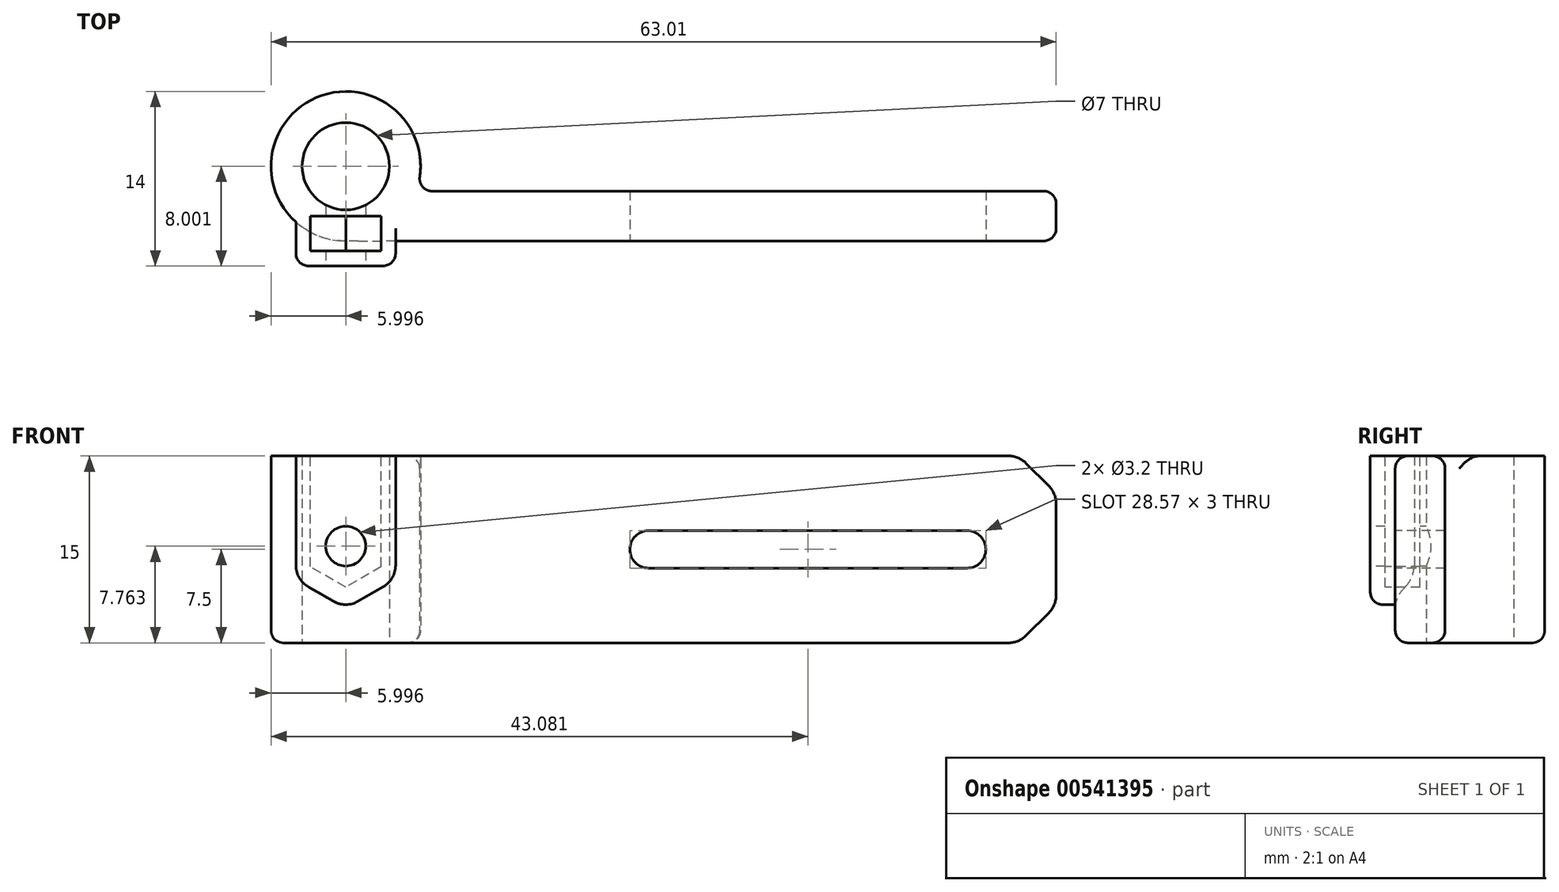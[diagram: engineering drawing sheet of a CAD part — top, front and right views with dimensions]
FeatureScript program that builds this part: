
annotation { "Feature Type Name" : "Feature", "Feature Type Description" : "" }
export const myFeature = defineFeature(function(context is Context, id is Id, definition is map)
    precondition{}
    {
        {
            var Q0;
            Q0=qCreatedBy(makeId("Top.planeOp"),FACE);
            var sketch = newSketch(context, id + "F0", { "sketchPlane" : qUnion([Q0])});
            skCircle(sketch, "E0", {"center": v(-30.85, 2.7) * mm, "radius": 3.5 * mm});
            skCircle(sketch, "E1", {"center": v(-30.85, 2.7) * mm, "radius": 6 * mm});
            skLineSegment(sketch, "E2", {"start": v(-30.85, -3.3) * mm, "end": v(26.16, -3.3) * mm});
            skLineSegment(sketch, "E3", {"start": v(26.16, -3.3) * mm, "end": v(26.16, 0.7) * mm});
            skLineSegment(sketch, "E4", {"start": v(26.16, 0.7) * mm, "end": v(-25.2, 0.7) * mm});
            skSolve(sketch);
        }
        {
            var Q0;
            {var subQ0=sQuery(id+"F0.wireOp",EDGE,"E2");Q0=makeQuery(id+"F0.imprint","IMPRINT",FACE,{"disambiguationData":[TD([[makeQuery(id+"F0.imprint","IMPRINT",EDGE,{"derivedFrom":subQ0}),1.0]])]});}
            var Q1;
            Q1=makeQuery(id+"F0.imprint","IMPRINT",FACE,{"disambiguationData":[TD([[makeQuery(id+"F0.imprint","IMPRINT",EDGE,{"derivedFrom":sQuery(id+"F0.wireOp",EDGE,"E0")}),-1.0]])]});
            extrude(context, id + "F1", {"entities" : qUnion([Q0, Q1]), "depth" : 15 * mm});
        }
        {
            var Q0;
            Q0=makeQuery(id+"F1.opExtrude","SWEPT_FACE",FACE,{"disambiguationData":[OSD([sQuery(id+"F0.wireOp",EDGE,"E2")])]});
            var sketch = newSketch(context, id + "F2", { "sketchPlane" : qUnion([Q0])});
            skCircle(sketch, "E5.cCircle", {"center": v(-30.85, 7.38) * mm, "radius": 4 * mm, "construction": true});
            skLineSegment(sketch, "E5.0", {"start": v(-26.85, 9.7) * mm, "end": v(-26.85, 5.07) * mm});
            skLineSegment(sketch, "E5.1", {"start": v(-26.85, 5.07) * mm, "end": v(-30.85, 2.76) * mm});
            skLineSegment(sketch, "E5.2", {"start": v(-30.85, 2.76) * mm, "end": v(-34.85, 5.07) * mm});
            skLineSegment(sketch, "E5.3", {"start": v(-34.85, 5.07) * mm, "end": v(-34.85, 9.7) * mm});
            skLineSegment(sketch, "E5.4", {"start": v(-34.85, 9.7) * mm, "end": v(-30.85, 12) * mm});
            skLineSegment(sketch, "E5.5", {"start": v(-30.85, 12) * mm, "end": v(-26.85, 9.7) * mm});
            skPoint(sketch, "E5.0.midPoint", {"position": v(-26.85, 7.38) * mm});
            skLineSegment(sketch, "E6", {"start": v(-34.85, 9.7) * mm, "end": v(-34.85, 15) * mm});
            skLineSegment(sketch, "E7", {"start": v(-34.85, 15) * mm, "end": v(-26.85, 15) * mm});
            skLineSegment(sketch, "E8", {"start": v(-26.85, 15) * mm, "end": v(-26.85, 9.7) * mm});
            skSolve(sketch);
        }
        {
            var Q0;
            Q0=makeQuery(id+"F2.imprint","IMPRINT",FACE,{"disambiguationData":[TD([[makeQuery(id+"F2.imprint","IMPRINT",EDGE,{"derivedFrom":sQuery(id+"F2.wireOp",EDGE,"E5.0")}),-1.0]])]});
            var Q1;
            {var subQ0=sQuery(id+"F2.wireOp",EDGE,"E5.2");Q1=makeQuery(id+"F2.imprint","IMPRINT",FACE,{"disambiguationData":[TD([[makeQuery(id+"F2.imprint","IMPRINT",EDGE,{"derivedFrom":subQ0}),-1.0]])]});}
            var Q2;
            {var subQ0=sQuery(id+"F2.wireOp",EDGE,"E5.5");Q2=makeQuery(id+"F2.imprint","IMPRINT",FACE,{"disambiguationData":[TD([[makeQuery(id+"F2.imprint","IMPRINT",EDGE,{"derivedFrom":subQ0}),1.0]])]});}
            var Q3;
            {var subQ0=sQuery(id+"F2.wireOp",EDGE,"E5.4");Q3=makeQuery(id+"F2.imprint","IMPRINT",FACE,{"disambiguationData":[TD([[makeQuery(id+"F2.imprint","IMPRINT",EDGE,{"derivedFrom":subQ0}),1.0]])]});}
            extrude(context, id + "F3", {"entities" : qUnion([Q0, Q1, Q2, Q3]), "operationType" : NewBodyOperationType.ADD, "oppositeDirection" : true, "depth" : 2 * mm, "hasSecondDirection" : true, "secondDirectionOppositeDirection" : false, "secondDirectionDepth" : 2 * mm});
        }
        {
            var Q0;
            Q0=makeQuery(id+"F3.opExtrude","CAP_FACE",FACE,{"disambiguationData":[OSD([sQuery(id+"F2.wireOp",EDGE,"E5.0"),sQuery(id+"F2.wireOp",EDGE,"E5.1"),sQuery(id+"F2.wireOp",EDGE,"E5.2"),sQuery(id+"F2.wireOp",EDGE,"E5.3"),sQuery(id+"F2.wireOp",EDGE,"E6"),sQuery(id+"F2.wireOp",EDGE,"E7"),sQuery(id+"F2.wireOp",EDGE,"E8")])],"isStart":true});
            var sketch = newSketch(context, id + "F4", { "sketchPlane" : qUnion([Q0])});
            skCircle(sketch, "E9.cCircle", {"center": v(-30.85, 7.76) * mm, "radius": 2.85 * mm, "construction": true});
            skLineSegment(sketch, "E9.0", {"start": v(-28, 9.4) * mm, "end": v(-28, 6.12) * mm});
            skLineSegment(sketch, "E9.1", {"start": v(-28, 6.12) * mm, "end": v(-30.85, 4.47) * mm});
            skLineSegment(sketch, "E9.2", {"start": v(-30.85, 4.47) * mm, "end": v(-33.7, 6.12) * mm});
            skLineSegment(sketch, "E9.3", {"start": v(-33.7, 6.12) * mm, "end": v(-33.7, 9.4) * mm});
            skLineSegment(sketch, "E9.4", {"start": v(-33.7, 9.4) * mm, "end": v(-30.85, 11.05) * mm});
            skLineSegment(sketch, "E9.5", {"start": v(-30.85, 11.05) * mm, "end": v(-28, 9.4) * mm});
            skPoint(sketch, "E9.0.midPoint", {"position": v(-28, 7.76) * mm});
            skLineSegment(sketch, "E10", {"start": v(-33.7, 9.4) * mm, "end": v(-33.7, 15) * mm});
            skLineSegment(sketch, "E11", {"start": v(-28, 9.4) * mm, "end": v(-28, 15) * mm});
            skSolve(sketch);
        }
        {
            var Q0;
            Q0=makeQuery(id+"F4.imprint","IMPRINT",FACE,{"disambiguationData":[TD([[makeQuery(id+"F4.imprint","IMPRINT",EDGE,{"derivedFrom":sQuery(id+"F4.wireOp",EDGE,"E9.4")}),1.0]])]});
            var Q1;
            Q1=makeQuery(id+"F4.imprint","IMPRINT",FACE,{"disambiguationData":[TD([[makeQuery(id+"F4.imprint","IMPRINT",EDGE,{"derivedFrom":sQuery(id+"F4.wireOp",EDGE,"E9.0")}),-1.0]])]});
            extrude(context, id + "F5", {"entities" : qUnion([Q0, Q1]), "operationType" : NewBodyOperationType.REMOVE, "oppositeDirection" : true, "depth" : 4 * mm, "hasSecondDirection" : true, "secondDirectionOppositeDirection" : true, "secondDirectionDepth" : 1.2 * mm});
        }
        {
            var Q0;
            Q0=sQuery(id+"F4.wireOp",VERTEX,"E9.cCircle.center");
            var Q1;
            Q1=makeQuery(id+"F1.opExtrude","SWEPT_BODY",BODY,{"disambiguationData":[OSD([sQuery(id+"F0.wireOp",EDGE,"E0"),sQuery(id+"F0.wireOp",EDGE,"E1"),sQuery(id+"F0.wireOp",EDGE,"E2"),sQuery(id+"F0.wireOp",EDGE,"E3"),sQuery(id+"F0.wireOp",EDGE,"E4")])]});
            hole(context, id + "F6", {"style" : HoleStyle.SIMPLE, "endStyle" : HoleEndStyle.BLIND, "holeDiameter" : 3.2 * mm, "holeDepth" : 8 * mm, "tappedDepth" : 12 * mm, "tapClearance" : 3, "startFromSketch" : true, "locations" : qUnion([Q0]), "scope" : qUnion([Q1])});
        }
        {
            var Q0;
            Q0=makeQuery(id+"F1.opExtrude","SWEPT_FACE",FACE,{"disambiguationData":[OSD([sQuery(id+"F0.wireOp",EDGE,"E2")])]});
            var sketch = newSketch(context, id + "F7", { "sketchPlane" : qUnion([Q0])});
            skCircle(sketch, "E12", {"center": v(-6.56, 7.5) * mm, "radius": 1.5 * mm});
            skPoint(sketch, "E12.centerSnap0", {"position": v(26.16, 7.5) * mm});
            skCircle(sketch, "E13", {"center": v(19.02, 7.5) * mm, "radius": 1.5 * mm});
            skLineSegment(sketch, "E14", {"start": v(-6.56, 6) * mm, "end": v(19.02, 6) * mm});
            skLineSegment(sketch, "E15", {"start": v(-6.56, 9) * mm, "end": v(19.02, 9) * mm});
            skSolve(sketch);
        }
        {
            var Q0;
            {var subQ0=sQuery(id+"F7.wireOp",EDGE,"E13");var subQ1=makeQuery(id+"F7.imprint","INTERSECT",VERTEX,{"derivedFrom":[subQ0,sQuery(id+"F7.wireOp",EDGE,"E14")]});Q0=makeQuery(id+"F7.imprint","IMPRINT",FACE,{"disambiguationData":[TD([[makeQuery(id+"F7.imprint","IMPRINT",EDGE,{"disambiguationData":[TD([[subQ1,1.0]])],"derivedFrom":subQ0}),1.0]])]});}
            var Q1;
            {var subQ0=sQuery(id+"F7.wireOp",EDGE,"E12");var subQ1=makeQuery(id+"F7.imprint","INTERSECT",VERTEX,{"derivedFrom":[subQ0,sQuery(id+"F7.wireOp",EDGE,"E14")]});Q1=makeQuery(id+"F7.imprint","IMPRINT",FACE,{"disambiguationData":[TD([[makeQuery(id+"F7.imprint","IMPRINT",EDGE,{"disambiguationData":[TD([[subQ1,1.0]])],"derivedFrom":subQ0}),1.0]])]});}
            var Q2;
            {var subQ0=sQuery(id+"F7.wireOp",EDGE,"E14");Q2=makeQuery(id+"F7.imprint","IMPRINT",FACE,{"disambiguationData":[TD([[makeQuery(id+"F7.imprint","IMPRINT",EDGE,{"derivedFrom":subQ0}),1.0]])]});}
            extrude(context, id + "F8", {"entities" : qUnion([Q0, Q1, Q2]), "operationType" : NewBodyOperationType.REMOVE, "oppositeDirection" : true, "depth" : 25 * mm});
        }
        {
            var Q0;
            Q0=makeQuery(id+"F1.opExtrude","CAP_EDGE",EDGE,{"disambiguationData":[OSD([sQuery(id+"F0.wireOp",EDGE,"E3")])],"isStart":false});
            var Q1;
            Q1=makeQuery(id+"F1.opExtrude","CAP_EDGE",EDGE,{"disambiguationData":[OSD([sQuery(id+"F0.wireOp",EDGE,"E3")])],"isStart":true});
            chamfer(context, id + "F9", {"entities" : qUnion([Q0, Q1]), "width" : 3 * mm, "tangentPropagation" : true});
        }
        {
            var Q0;
            Q0=makeQuery(id+"F3.opExtrude","SWEPT_EDGE",EDGE,{"disambiguationData":[OSD([sQuery(id+"F2.wireOp",EDGE,"E5.2"),sQuery(id+"F2.wireOp",EDGE,"E5.3")])]});
            var Q1;
            Q1=makeQuery(id+"F3.opExtrude","SWEPT_EDGE",EDGE,{"disambiguationData":[OSD([sQuery(id+"F0.wireOp",EDGE,"E1"),sQuery(id+"F0.wireOp",EDGE,"E2"),sQuery(id+"F2.wireOp",EDGE,"E5.1"),sQuery(id+"F2.wireOp",EDGE,"E5.2")])]});
            var Q2;
            Q2=makeQuery(id+"F3.opExtrude","SWEPT_EDGE",EDGE,{"disambiguationData":[OSD([sQuery(id+"F2.wireOp",EDGE,"E5.0"),sQuery(id+"F2.wireOp",EDGE,"E5.1")])]});
            var Q3;
            {var subQ0=sQuery(id+"F0.wireOp",EDGE,"E3");Q3=makeQuery(id+"F9.opChamfer","BLEND_EDGE",EDGE,{"blendedFrom":[makeQuery(id+"F1.opExtrude","CAP_EDGE",EDGE,{"disambiguationData":[OSD([subQ0])],"isStart":true}),makeQuery(id+"F1.opExtrude","CAP_FACE",FACE,{"disambiguationData":[OSD([sQuery(id+"F0.wireOp",EDGE,"E0"),sQuery(id+"F0.wireOp",EDGE,"E1"),sQuery(id+"F0.wireOp",EDGE,"E2"),subQ0,sQuery(id+"F0.wireOp",EDGE,"E4")])],"isStart":true})],"blendedInto":[makeQuery(id+"F1.opExtrude","CAP_FACE",FACE,{"disambiguationData":[OSD([sQuery(id+"F0.wireOp",EDGE,"E0"),sQuery(id+"F0.wireOp",EDGE,"E1"),sQuery(id+"F0.wireOp",EDGE,"E2"),subQ0,sQuery(id+"F0.wireOp",EDGE,"E4")])],"isStart":true})]});}
            var Q4;
            {var subQ0=sQuery(id+"F0.wireOp",EDGE,"E3");Q4=makeQuery(id+"F9.opChamfer","BLEND_EDGE",EDGE,{"blendedFrom":[makeQuery(id+"F1.opExtrude","CAP_EDGE",EDGE,{"disambiguationData":[OSD([subQ0])],"isStart":true}),makeQuery(id+"F1.opExtrude","SWEPT_FACE",FACE,{"disambiguationData":[OSD([subQ0])]})],"blendedInto":[makeQuery(id+"F1.opExtrude","SWEPT_FACE",FACE,{"disambiguationData":[OSD([subQ0])]})]});}
            var Q5;
            {var subQ0=sQuery(id+"F0.wireOp",EDGE,"E3");Q5=makeQuery(id+"F9.opChamfer","BLEND_EDGE",EDGE,{"blendedFrom":[makeQuery(id+"F1.opExtrude","CAP_EDGE",EDGE,{"disambiguationData":[OSD([subQ0])],"isStart":false}),makeQuery(id+"F1.opExtrude","SWEPT_FACE",FACE,{"disambiguationData":[OSD([subQ0])]})],"blendedInto":[makeQuery(id+"F1.opExtrude","SWEPT_FACE",FACE,{"disambiguationData":[OSD([subQ0])]})]});}
            var Q6;
            {var subQ0=sQuery(id+"F0.wireOp",EDGE,"E3");Q6=makeQuery(id+"F9.opChamfer","BLEND_EDGE",EDGE,{"blendedFrom":[makeQuery(id+"F1.opExtrude","CAP_EDGE",EDGE,{"disambiguationData":[OSD([subQ0])],"isStart":false}),makeQuery(id+"F3.boolean.opBoolean","MERGE",FACE,{"derivedFrom":[makeQuery(id+"F1.opExtrude","CAP_FACE",FACE,{"disambiguationData":[OSD([sQuery(id+"F0.wireOp",EDGE,"E0"),sQuery(id+"F0.wireOp",EDGE,"E1"),sQuery(id+"F0.wireOp",EDGE,"E2"),subQ0,sQuery(id+"F0.wireOp",EDGE,"E4")])],"isStart":false}),makeQuery(id+"F3.opExtrude","SWEPT_FACE",FACE,{"disambiguationData":[OSD([sQuery(id+"F2.wireOp",EDGE,"E7")])]})]})],"blendedInto":[makeQuery(id+"F3.boolean.opBoolean","MERGE",FACE,{"derivedFrom":[makeQuery(id+"F1.opExtrude","CAP_FACE",FACE,{"disambiguationData":[OSD([sQuery(id+"F0.wireOp",EDGE,"E0"),sQuery(id+"F0.wireOp",EDGE,"E1"),sQuery(id+"F0.wireOp",EDGE,"E2"),subQ0,sQuery(id+"F0.wireOp",EDGE,"E4")])],"isStart":false}),makeQuery(id+"F3.opExtrude","SWEPT_FACE",FACE,{"disambiguationData":[OSD([sQuery(id+"F2.wireOp",EDGE,"E7")])]})]})]});}
            fillet(context, id + "F10", {"entities" : qUnion([Q0, Q1, Q2, Q3, Q4, Q5, Q6]), "radius" : 2 * mm, "tangentPropagation" : true, "allowEdgeOverflow" : false});
        }
        {
            var Q0;
            Q0=makeQuery(id+"F3.opExtrude","CAP_EDGE",EDGE,{"disambiguationData":[OSD([sQuery(id+"F2.wireOp",EDGE,"E5.3"),sQuery(id+"F2.wireOp",EDGE,"E6")])],"isStart":true});
            var Q1;
            Q1=makeQuery(id+"F1.opExtrude","CAP_EDGE",EDGE,{"disambiguationData":[OSD([sQuery(id+"F0.wireOp",EDGE,"E2")])],"isStart":false});
            var Q2;
            Q2=makeQuery(id+"F1.opExtrude","CAP_EDGE",EDGE,{"disambiguationData":[OSD([sQuery(id+"F0.wireOp",EDGE,"E4")])],"isStart":true});
            var Q3;
            Q3=makeQuery(id+"F1.opExtrude","SWEPT_EDGE",EDGE,{"disambiguationData":[OSD([sQuery(id+"F0.wireOp",EDGE,"E1"),sQuery(id+"F0.wireOp",EDGE,"E4")])]});
            fillet(context, id + "F11", {"entities" : qUnion([Q0, Q1, Q2, Q3]), "radius" : 1 * mm, "tangentPropagation" : true, "allowEdgeOverflow" : false});
        }
    });
